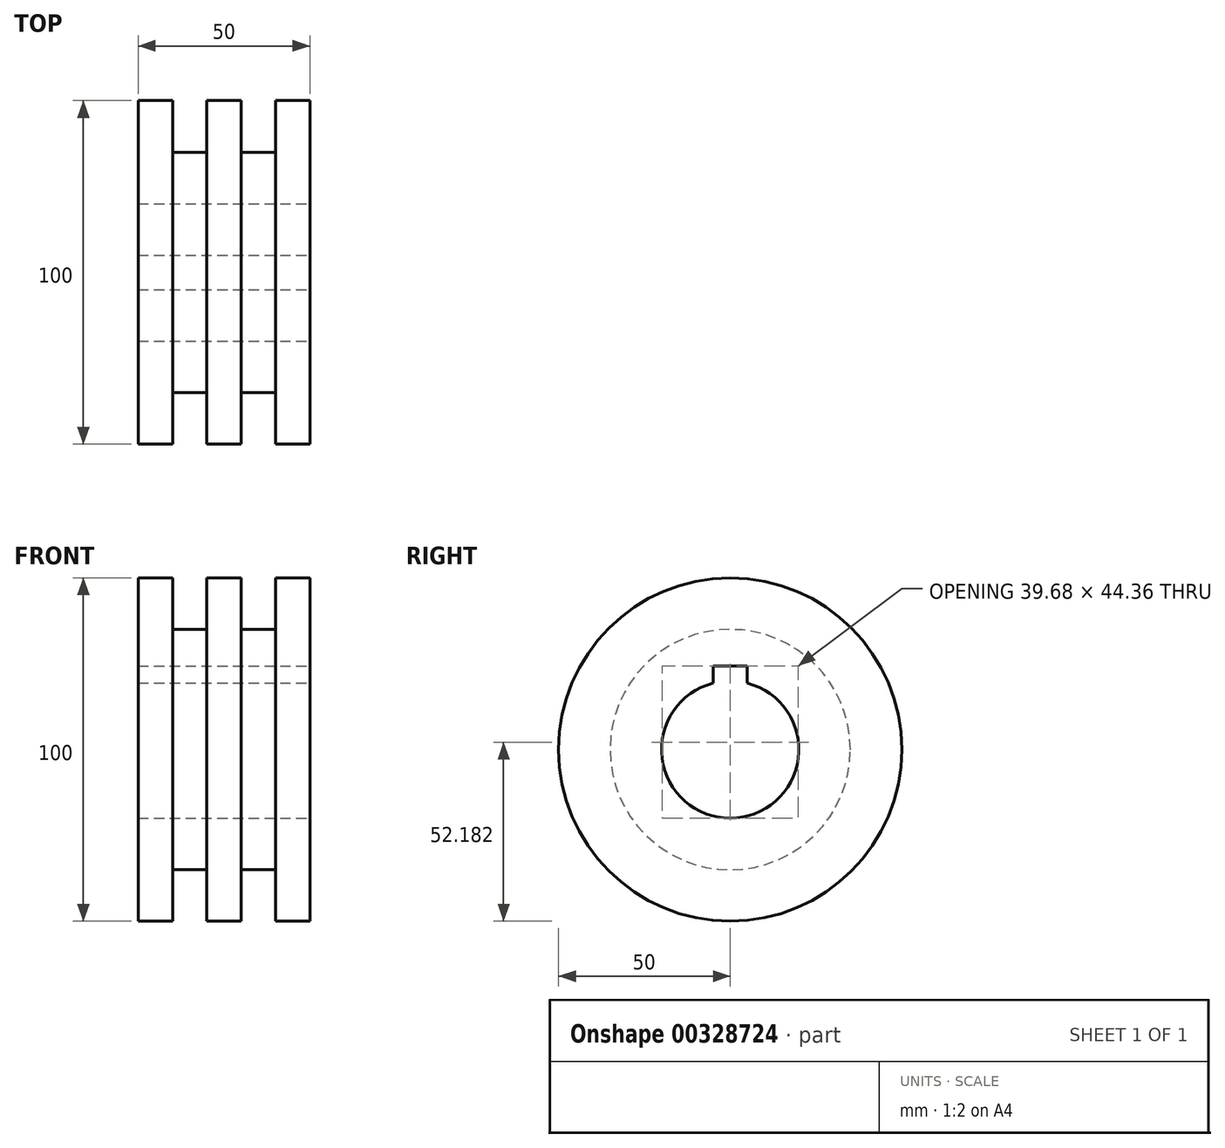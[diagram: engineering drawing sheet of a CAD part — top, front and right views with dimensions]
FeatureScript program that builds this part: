
annotation { "Feature Type Name" : "Feature", "Feature Type Description" : "" }
export const myFeature = defineFeature(function(context is Context, id is Id, definition is map)
    precondition{}
    {
        {
            var Q0;
            Q0=qCreatedBy(makeId("Top.planeOp"),FACE);
            var sketch = newSketch(context, id + "F0", { "sketchPlane" : qUnion([Q0])});
            skLineSegment(sketch, "E0.bottom", {"start": v(25, -25) * mm, "end": v(15, -25) * mm});
            skLineSegment(sketch, "E0.top", {"start": v(25, 25) * mm, "end": v(-25, 25) * mm});
            skLineSegment(sketch, "E0.left", {"start": v(25, -25) * mm, "end": v(25, 25) * mm});
            skLineSegment(sketch, "E0.right", {"start": v(-25, -25) * mm, "end": v(-25, 25) * mm});
            skPoint(sketch, "E0.middle", {"position": v(0, 0) * mm});
            skLineSegment(sketch, "E1", {"start": v(-15, -25) * mm, "end": v(-15, -10) * mm});
            skLineSegment(sketch, "E2", {"start": v(-15, -10) * mm, "end": v(-5, -10) * mm});
            skLineSegment(sketch, "E3", {"start": v(-5, -10) * mm, "end": v(-5, -25) * mm});
            skLineSegment(sketch, "E4", {"start": v(5, -25) * mm, "end": v(5, -10) * mm});
            skLineSegment(sketch, "E5", {"start": v(5, -10) * mm, "end": v(15, -10) * mm});
            skLineSegment(sketch, "E6", {"start": v(15, -10) * mm, "end": v(15, -25) * mm});
            skLineSegment(sketch, "E7.trimOffspring", {"start": v(-15, -25) * mm, "end": v(-25, -25) * mm});
            skLineSegment(sketch, "E8.trimOffspring", {"start": v(5, -25) * mm, "end": v(-5, -25) * mm});
            skSolve(sketch);
        }
        {
            var Q0;
            Q0=makeQuery(id+"F0.imprint","IMPRINT",FACE,{"disambiguationData":[TD([[makeQuery(id+"F0.imprint","IMPRINT",EDGE,{"derivedFrom":sQuery(id+"F0.wireOp",EDGE,"E0.bottom")}),-1.0]])]});
            var Q1;
            Q1=sQuery(id+"F0.wireOp",EDGE,"E0.top");
            revolve(context, id + "F1", {"entities" : qUnion([Q0]), "axis" : qUnion([Q1]), "revolveType" : RevolveType.FULL});
        }
        {
            var Q0;
            Q0=makeQuery(id+"F1.opRevolve","SWEPT_FACE",FACE,{"disambiguationData":[OSD([sQuery(id+"F0.wireOp",EDGE,"E0.left")])]});
            var sketch = newSketch(context, id + "F2", { "sketchPlane" : qUnion([Q0])});
            skArc(sketch, "E9", {"start": v(20, 19.36) * mm, "mid": v(25, -20) * mm, "end": v(30, 19.36) * mm});
            skLineSegment(sketch, "E10", {"start": v(25, 24.36) * mm, "end": v(20, 24.36) * mm});
            skLineSegment(sketch, "E11", {"start": v(20, 24.36) * mm, "end": v(20, 19.36) * mm});
            skLineSegment(sketch, "E12", {"start": v(25, 24.36) * mm, "end": v(30, 24.36) * mm});
            skLineSegment(sketch, "E13", {"start": v(30, 24.36) * mm, "end": v(30, 19.36) * mm});
            skPoint(sketch, "E14.start.orphan", {"position": v(25, 20) * mm});
            skSolve(sketch);
        }
        {
            var Q0;
            Q0=makeQuery(id+"F2.imprint","IMPRINT",FACE,{"disambiguationData":[TD([[makeQuery(id+"F2.imprint","IMPRINT",EDGE,{"derivedFrom":sQuery(id+"F2.wireOp",EDGE,"E9")}),1.0]])]});
            extrude(context, id + "F3", {"entities" : qUnion([Q0]), "operationType" : NewBodyOperationType.REMOVE, "oppositeDirection" : true, "depth" : 50 * mm});
        }
    });
